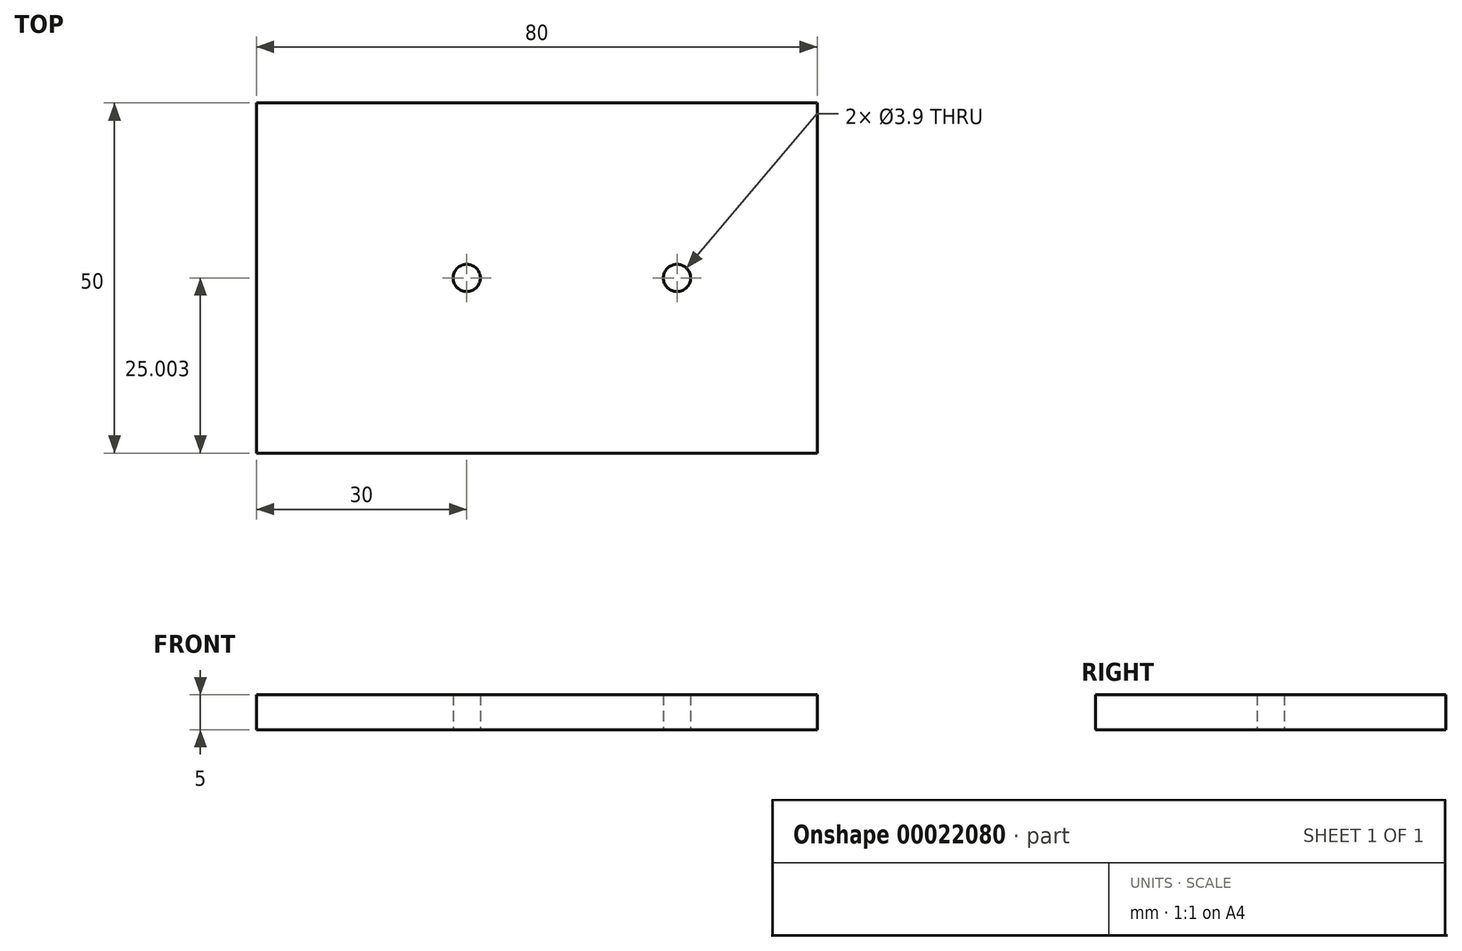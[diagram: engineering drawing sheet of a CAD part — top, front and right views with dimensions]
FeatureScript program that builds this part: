
annotation { "Feature Type Name" : "Feature", "Feature Type Description" : "" }
export const myFeature = defineFeature(function(context is Context, id is Id, definition is map)
    precondition{}
    {
        {
            var Q0;
            Q0=qCreatedBy(makeId("Top.planeOp"),FACE);
            var sketch = newSketch(context, id + "F0", { "sketchPlane" : qUnion([Q0])});
            skLineSegment(sketch, "E0.bottom", {"start": v(-38.68, 23.52) * mm, "end": v(41.32, 23.52) * mm});
            skLineSegment(sketch, "E0.top", {"start": v(-38.68, -26.48) * mm, "end": v(41.32, -26.48) * mm});
            skLineSegment(sketch, "E0.left", {"start": v(-38.68, 23.52) * mm, "end": v(-38.68, -26.48) * mm});
            skLineSegment(sketch, "E0.right", {"start": v(41.32, 23.52) * mm, "end": v(41.32, -26.48) * mm});
            skCircle(sketch, "E1", {"center": v(-8.68, -1.48) * mm, "radius": 1.95 * mm});
            skCircle(sketch, "E2", {"center": v(21.32, -1.48) * mm, "radius": 1.95 * mm});
            skSolve(sketch);
        }
        {
            var Q0;
            Q0=makeQuery(id+"F0.imprint","IMPRINT",FACE,{"disambiguationData":[TD([[makeQuery(id+"F0.imprint","IMPRINT",EDGE,{"derivedFrom":sQuery(id+"F0.wireOp",EDGE,"E0.bottom")}),-1.0]])]});
            extrude(context, id + "F1", {"entities" : qUnion([Q0]), "endBound" : BoundingType.SYMMETRIC, "depth" : 5 * mm});
        }
    });
